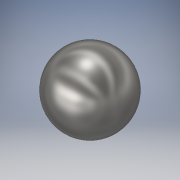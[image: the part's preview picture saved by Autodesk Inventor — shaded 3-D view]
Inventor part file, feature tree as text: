
AUTODESK INVENTOR PART (.ipt)
format: ipt  version: 2018 (Build 220112000, 112)  size: 127,488 bytes
history: native  units: in
note: dims shown in document units (in); Inventor stores cm internally (conversion verified against a paired STEP export)
features: revolve x1, sketch x1
ambient origin geometry x8: Origin, YZ Plane, XZ Plane, XY Plane, X Axis, Y Axis, Z Axis, Center Point
bodies: Solid1 (feature_tree)
feature tree (2):
  revolve  "Revolution1"  Angle=90.0deg
  sketch  "Sketch1"  dims[d0=0.375in d1=90.0deg]
